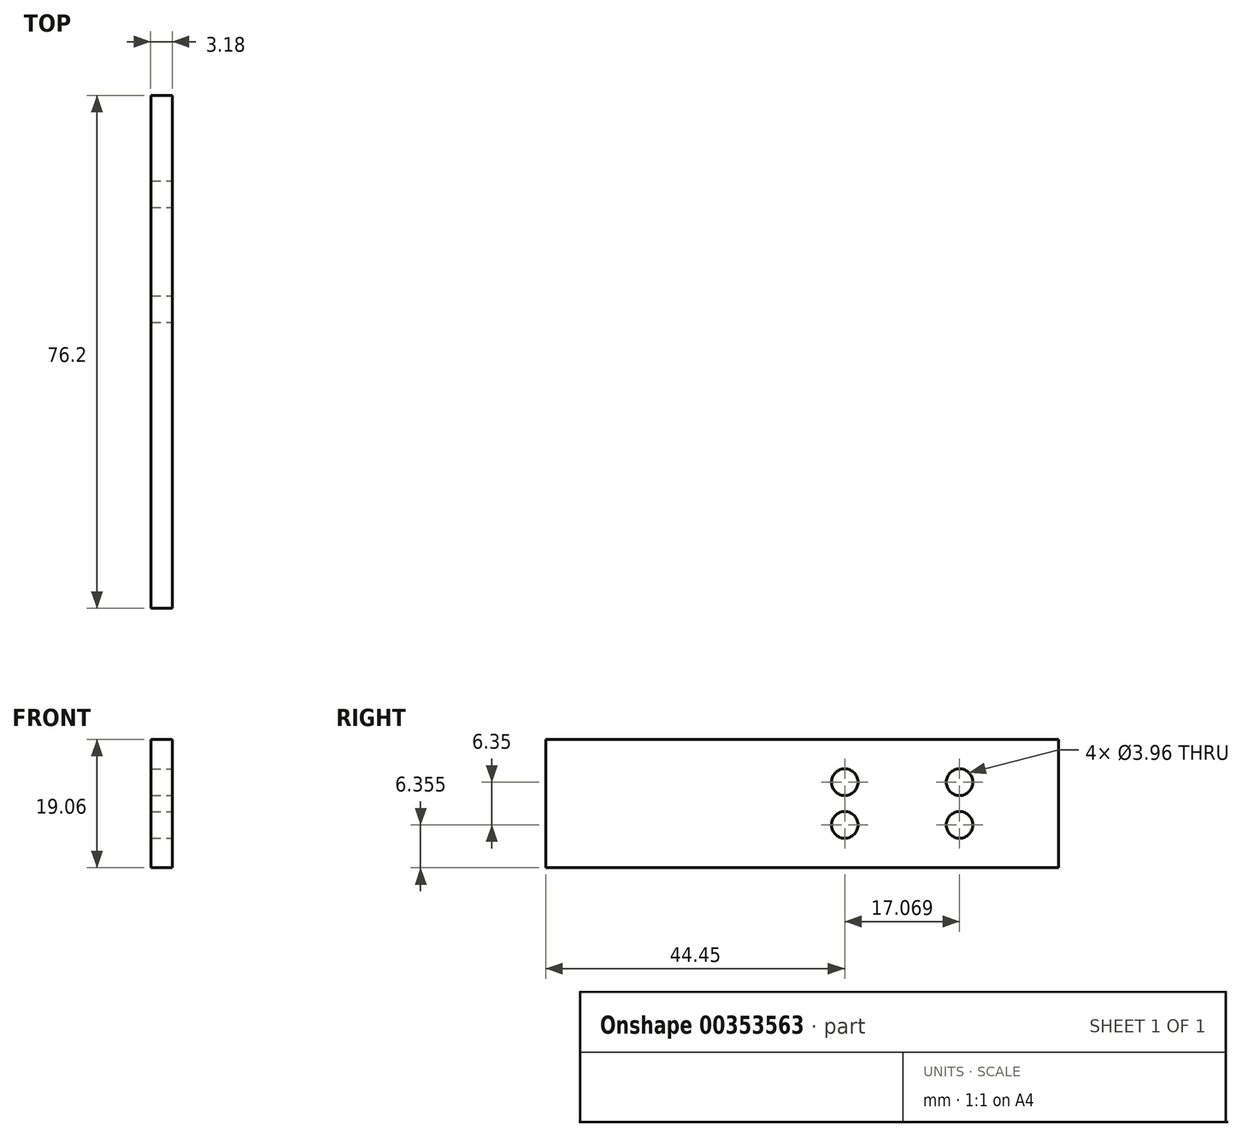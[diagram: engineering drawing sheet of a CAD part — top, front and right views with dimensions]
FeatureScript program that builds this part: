
annotation { "Feature Type Name" : "Feature", "Feature Type Description" : "" }
export const myFeature = defineFeature(function(context is Context, id is Id, definition is map)
    precondition{}
    {
        {
            var Q0;
            Q0=qCreatedBy(makeId("Front.planeOp"),FACE);
            var sketch = newSketch(context, id + "F0", { "sketchPlane" : qUnion([Q0])});
            skLineSegment(sketch, "E0.bottom", {"start": v(1.59, 9.52) * mm, "end": v(-1.59, 9.52) * mm});
            skLineSegment(sketch, "E0.top", {"start": v(1.59, -9.53) * mm, "end": v(-1.59, -9.53) * mm});
            skLineSegment(sketch, "E0.left", {"start": v(1.59, 9.52) * mm, "end": v(1.59, -9.53) * mm});
            skLineSegment(sketch, "E0.right", {"start": v(-1.59, 9.52) * mm, "end": v(-1.59, -9.53) * mm});
            skPoint(sketch, "E0.middle", {"position": v(0, 0) * mm});
            skSolve(sketch);
        }
        {
            var Q0;
            Q0 = qSketchRegion(id + "F0", true);
            extrude(context, id + "F1", {"entities" : qUnion([Q0]), "depth" : 76.2 * mm, "symmetric" : true});
        }
        {
            var Q0;
            Q0=makeQuery(id+"F1.opExtrude","SWEPT_FACE",FACE,{"disambiguationData":[OSD([sQuery(id+"F0.wireOp",EDGE,"E0.left")])]});
            var sketch = newSketch(context, id + "F2", { "sketchPlane" : qUnion([Q0])});
            skCircle(sketch, "E1", {"center": v(23.42, 3.17) * mm, "radius": 1.98 * mm});
            skCircle(sketch, "E2", {"center": v(23.42, -3.17) * mm, "radius": 1.98 * mm});
            skSolve(sketch);
        }
        {
            var Q0;
            Q0 = qSketchRegion(id + "F2", true);
            extrude(context, id + "F3", {"entities" : qUnion([Q0]), "operationType" : NewBodyOperationType.REMOVE, "endBound" : BoundingType.THROUGH_ALL, "oppositeDirection" : true, "depth" : 25.4 * mm});
        }
        {
            var Q0;
            Q0=makeQuery(id+"F1.opExtrude","SWEPT_FACE",FACE,{"disambiguationData":[OSD([sQuery(id+"F0.wireOp",EDGE,"E0.left")])]});
            var sketch = newSketch(context, id + "F4", { "sketchPlane" : qUnion([Q0])});
            skCircle(sketch, "E3", {"center": v(6.35, 3.17) * mm, "radius": 1.98 * mm});
            skCircle(sketch, "E4", {"center": v(6.35, -3.17) * mm, "radius": 1.98 * mm});
            skSolve(sketch);
        }
        {
            var Q0;
            Q0 = qSketchRegion(id + "F4", true);
            extrude(context, id + "F5", {"entities" : qUnion([Q0]), "operationType" : NewBodyOperationType.REMOVE, "endBound" : BoundingType.THROUGH_ALL, "oppositeDirection" : true, "depth" : 25.4 * mm});
        }
    });
